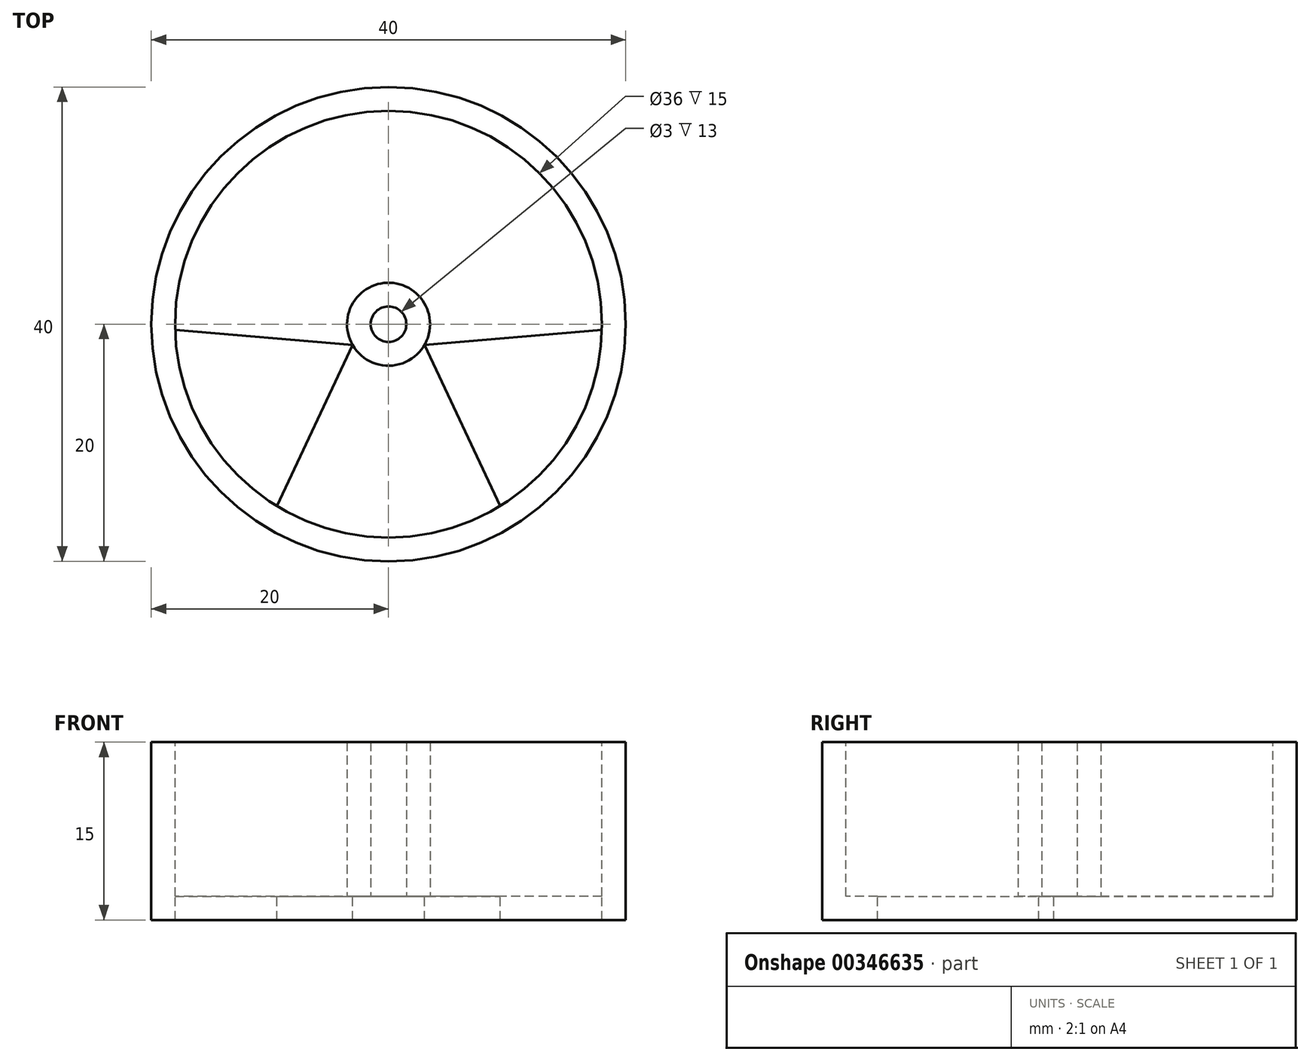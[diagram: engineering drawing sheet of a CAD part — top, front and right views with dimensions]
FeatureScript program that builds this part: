
annotation { "Feature Type Name" : "Feature", "Feature Type Description" : "" }
export const myFeature = defineFeature(function(context is Context, id is Id, definition is map)
    precondition{}
    {
        {
            var Q0;
            Q0=qCreatedBy(makeId("Top.planeOp"),FACE);
            var sketch = newSketch(context, id + "F0", { "sketchPlane" : qUnion([Q0])});
            skCircle(sketch, "E0", {"center": v(0, 0) * mm, "radius": 20 * mm});
            skSolve(sketch);
        }
        {
            var Q0;
            Q0=makeQuery(id+"F0.imprint","IMPRINT",FACE,{"disambiguationData":[TD([[makeQuery(id+"F0.imprint","IMPRINT",EDGE,{"derivedFrom":sQuery(id+"F0.wireOp",EDGE,"E0")}),1.0]])]});
            extrude(context, id + "F1", {"entities" : qUnion([Q0]), "depth" : 15 * mm});
        }
        {
            var Q0;
            Q0=makeQuery(id+"F1.opExtrude","CAP_FACE",FACE,{"disambiguationData":[OSD([sQuery(id+"F0.wireOp",EDGE,"E0")])],"isStart":false});
            var sketch = newSketch(context, id + "F2", { "sketchPlane" : qUnion([Q0])});
            skCircle(sketch, "E1", {"center": v(0, 0) * mm, "radius": 18 * mm});
            skSolve(sketch);
        }
        {
            var Q0;
            Q0=makeQuery(id+"F2.imprint","IMPRINT",FACE,{"disambiguationData":[TD([[makeQuery(id+"F2.imprint","IMPRINT",EDGE,{"derivedFrom":sQuery(id+"F2.wireOp",EDGE,"E1")}),1.0]])]});
            extrude(context, id + "F3", {"entities" : qUnion([Q0]), "operationType" : NewBodyOperationType.REMOVE, "oppositeDirection" : true, "depth" : 13 * mm});
        }
        {
            var Q0;
            Q0=makeQuery(id+"F3.boolean.opBoolean","COPY",FACE,{"derivedFrom":makeQuery(id+"F3.opExtrude","CAP_FACE",FACE,{"disambiguationData":[OSD([sQuery(id+"F2.wireOp",EDGE,"E1")])],"isStart":false})});
            var sketch = newSketch(context, id + "F4", { "sketchPlane" : qUnion([Q0])});
            skCircle(sketch, "E2", {"center": v(0, 0) * mm, "radius": 3.5 * mm});
            skCircle(sketch, "E3", {"center": v(0, 0) * mm, "radius": 1.5 * mm});
            skSolve(sketch);
        }
        {
            var Q0;
            Q0 = qSketchRegion(id + "F4", true);
            extrude(context, id + "F5", {"entities" : qUnion([Q0]), "operationType" : NewBodyOperationType.ADD, "depth" : 13 * mm});
        }
        {
            var Q0;
            {var subQ0=sQuery(id+"F2.wireOp",EDGE,"E1");Q0=makeQuery(id+"F5.boolean.opBoolean","SPLIT",FACE,{"disambiguationData":[TD([makeQuery(id+"F3.boolean.opBoolean","COPY",FACE,{"derivedFrom":makeQuery(id+"F3.opExtrude","SWEPT_FACE",FACE,{"disambiguationData":[OSD([subQ0])]})})])],"derivedFrom":makeQuery(id+"F3.boolean.opBoolean","COPY",FACE,{"derivedFrom":makeQuery(id+"F3.opExtrude","CAP_FACE",FACE,{"disambiguationData":[OSD([subQ0])],"isStart":false})})});}
            var sketch = newSketch(context, id + "F6", { "sketchPlane" : qUnion([Q0])});
            skLineSegment(sketch, "E4", {"start": v(0, 3.5) * mm, "end": v(-8.57, 15.83) * mm});
            skLineSegment(sketch, "E5", {"start": v(-8.57, 15.83) * mm, "end": v(0, 3.5) * mm});
            skLineSegment(sketch, "E6", {"start": v(0, 3.5) * mm, "end": v(8.57, 15.83) * mm});
            skLineSegment(sketch, "E7", {"start": v(8.57, 15.83) * mm, "end": v(0, 3.5) * mm});
            skLineSegment(sketch, "E8.1.0", {"start": v(-18, -0.5) * mm, "end": v(-3.03, -1.75) * mm});
            skLineSegment(sketch, "E8.1.1", {"start": v(-9.42, -15.34) * mm, "end": v(-3.03, -1.75) * mm});
            skLineSegment(sketch, "E8.2.0", {"start": v(9.42, -15.34) * mm, "end": v(3.03, -1.75) * mm});
            skLineSegment(sketch, "E8.2.1", {"start": v(18, -0.5) * mm, "end": v(3.03, -1.75) * mm});
            skPoint(sketch, "E8.center", {"position": v(0, 0) * mm});
            skSolve(sketch);
        }
        {
            var Q0;
            {var subQ0=sQuery(id+"F6.wireOp",EDGE,"E8.1.0");Q0=makeQuery(id+"F6.imprint","IMPRINT",FACE,{"disambiguationData":[TD([[makeQuery(id+"F6.imprint","IMPRINT",EDGE,{"derivedFrom":subQ0}),-1.0]])]});}
            var Q1;
            {var subQ0=sQuery(id+"F6.wireOp",EDGE,"E5");Q1=makeQuery(id+"F6.imprint","IMPRINT",FACE,{"disambiguationData":[TD([[makeQuery(id+"F6.imprint","IMPRINT",EDGE,{"derivedFrom":subQ0}),1.0]])]});}
            var Q2;
            {var subQ0=sQuery(id+"F6.wireOp",EDGE,"E8.2.0");Q2=makeQuery(id+"F6.imprint","IMPRINT",FACE,{"disambiguationData":[TD([[makeQuery(id+"F6.imprint","IMPRINT",EDGE,{"derivedFrom":subQ0}),-1.0]])]});}
            extrude(context, id + "F7", {"entities" : qUnion([Q0, Q1, Q2]), "operationType" : NewBodyOperationType.REMOVE, "oppositeDirection" : true, "depth" : 100 * mm});
        }
    });
